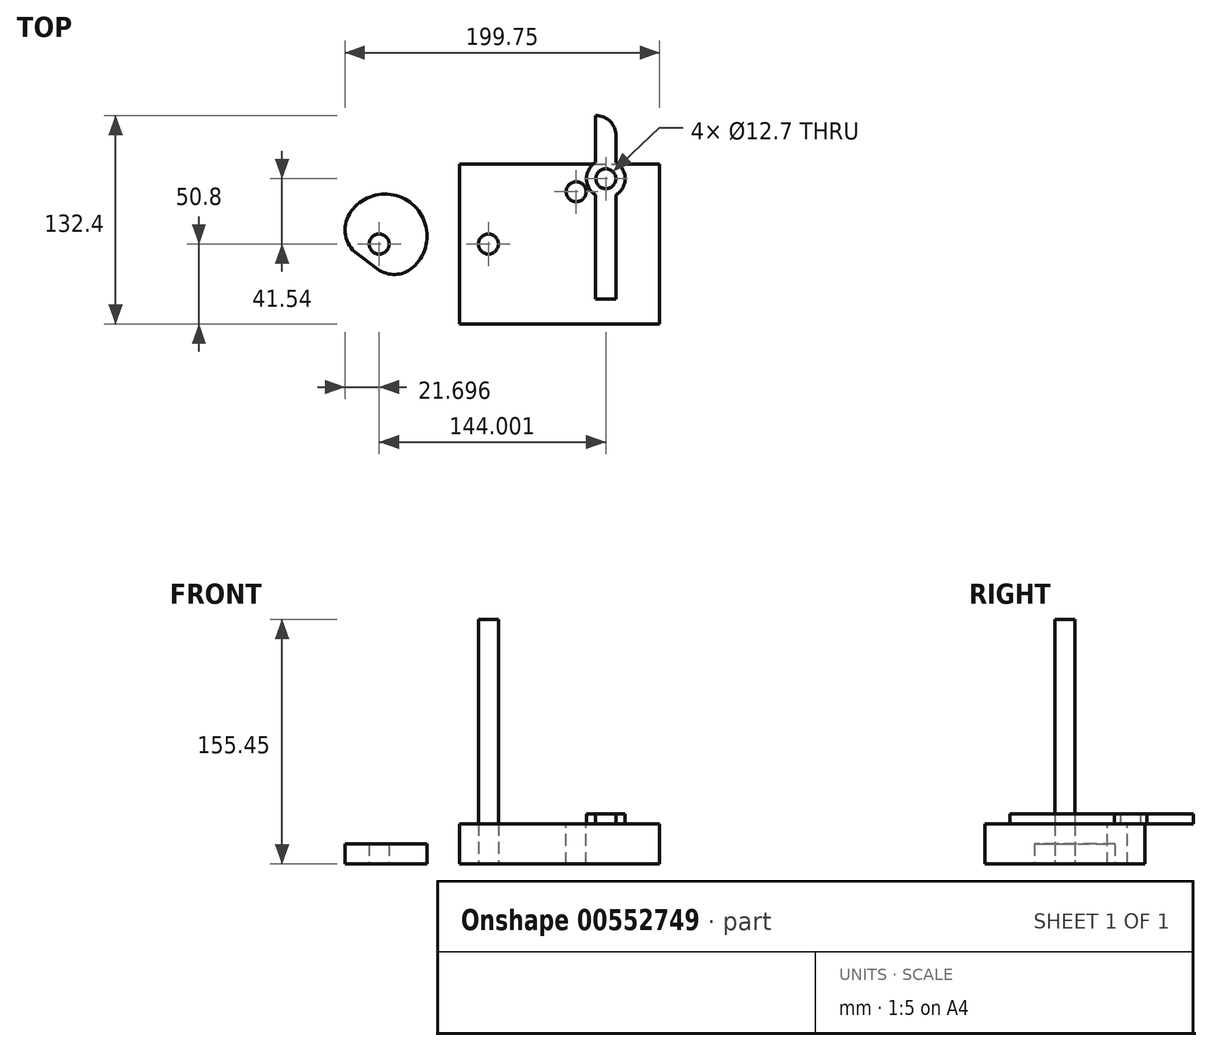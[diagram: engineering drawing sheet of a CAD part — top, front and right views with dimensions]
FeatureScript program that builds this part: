
annotation { "Feature Type Name" : "Feature", "Feature Type Description" : "" }
export const myFeature = defineFeature(function(context is Context, id is Id, definition is map)
    precondition{}
    {
        {
            var Q0;
            Q0=qCreatedBy(makeId("Top.planeOp"),FACE);
            var sketch = newSketch(context, id + "F0", { "sketchPlane" : qUnion([Q0])});
            skLineSegment(sketch, "E0.bottom", {"start": v(-63.5, -50.8) * mm, "end": v(63.5, -50.8) * mm});
            skLineSegment(sketch, "E0.top", {"start": v(-63.5, 50.8) * mm, "end": v(63.5, 50.8) * mm});
            skLineSegment(sketch, "E0.left", {"start": v(-63.5, -50.8) * mm, "end": v(-63.5, 50.8) * mm});
            skLineSegment(sketch, "E0.right", {"start": v(63.5, -50.8) * mm, "end": v(63.5, 50.8) * mm});
            skPoint(sketch, "E0.middle", {"position": v(0, 0) * mm});
            skCircle(sketch, "E1", {"center": v(-45.14, 0) * mm, "radius": 6.35 * mm});
            skSolve(sketch);
        }
        {
            var Q0;
            Q0=makeQuery(id+"F0.imprint","IMPRINT",FACE,{"disambiguationData":[TD([[makeQuery(id+"F0.imprint","IMPRINT",EDGE,{"derivedFrom":sQuery(id+"F0.wireOp",EDGE,"E0.bottom")}),1.0]])]});
            extrude(context, id + "F1", {"entities" : qUnion([Q0]), "depth" : 25.4 * mm, "offsetDistance" : 25.4 * mm});
        }
        {
            var Q0;
            Q0=makeQuery(id+"F1.opExtrude","CAP_FACE",FACE,{"disambiguationData":[OSD([sQuery(id+"F0.wireOp",EDGE,"E0.bottom"),sQuery(id+"F0.wireOp",EDGE,"E0.top"),sQuery(id+"F0.wireOp",EDGE,"E0.left"),sQuery(id+"F0.wireOp",EDGE,"E0.right"),sQuery(id+"F0.wireOp",EDGE,"E1")])],"isStart":false});
            var sketch = newSketch(context, id + "F2", { "sketchPlane" : qUnion([Q0])});
            skCircle(sketch, "E2.0", {"center": v(-45.14, 0) * mm, "radius": 6.35 * mm});
            skSolve(sketch);
        }
        {
            var Q0;
            Q0 = qSketchRegion(id + "F2", true);
            extrude(context, id + "F3", {"entities" : qUnion([Q0]), "depth" : 130.05 * mm, "offsetDistance" : 25.4 * mm});
        }
        {
            var Q0;
            Q0=qCreatedBy(makeId("Top.planeOp"),FACE);
            var sketch = newSketch(context, id + "F4", { "sketchPlane" : qUnion([Q0])});
            skArc(sketch, "E3", {"start": v(-108.1, -21.4) * mm, "mid": v(-101.23, 17.94) * mm, "end": v(-136.9, 0) * mm, "construction": true});
            skCircle(sketch, "E4", {"center": v(-114.55, 0) * mm, "radius": 6.35 * mm});
            skLineSegment(sketch, "E5", {"start": v(-136.9, 0) * mm, "end": v(-108.1, -21.4) * mm});
            skArc(sketch, "E6", {"start": v(-108.1, -21.4) * mm, "mid": v(-94.9, 26.48) * mm, "end": v(-136.9, 0) * mm});
            skSolve(sketch);
        }
        {
            var Q0;
            Q0=makeQuery(id+"F4.imprint","IMPRINT",FACE,{"disambiguationData":[TD([[makeQuery(id+"F4.imprint","IMPRINT",EDGE,{"derivedFrom":sQuery(id+"F4.wireOp",EDGE,"E4")}),-1.0]])]});
            extrude(context, id + "F5", {"entities" : qUnion([Q0]), "depth" : 12.7 * mm, "offsetDistance" : 25.4 * mm});
        }
        {
            var Q0;
            {var subQ0=sQuery(id+"F4.wireOp",EDGE,"E6");var subQ1=sQuery(id+"F4.wireOp",EDGE,"E5");Q0=makeQuery(id+"F5.opExtrude","SWEPT_EDGE",EDGE,{"disambiguationData":[OSD([subQ1,subQ0]),TDD([makeQuery(id+"F4.imprint","INTERSECT",VERTEX,{"disambiguationData":[OD(0.0)],"derivedFrom":[subQ1,subQ0]})])]});}
            fillet(context, id + "F6", {"entities" : qUnion([Q0]), "radius" : 19.05 * mm, "tangentPropagation" : true, "allowEdgeOverflow" : false});
        }
        {
            var Q0;
            {var subQ0=sQuery(id+"F4.wireOp",EDGE,"E6");var subQ1=sQuery(id+"F4.wireOp",EDGE,"E5");Q0=makeQuery(id+"F5.opExtrude","SWEPT_EDGE",EDGE,{"disambiguationData":[OSD([subQ1,subQ0]),TDD([makeQuery(id+"F4.imprint","INTERSECT",VERTEX,{"disambiguationData":[OD(1.0)],"derivedFrom":[subQ1,subQ0]})])]});}
            fillet(context, id + "F7", {"entities" : qUnion([Q0]), "radius" : 17.78 * mm, "tangentPropagation" : true, "allowEdgeOverflow" : false});
        }
        {
            var Q0;
            Q0=makeQuery(id+"F1.opExtrude","CAP_FACE",FACE,{"disambiguationData":[OSD([sQuery(id+"F0.wireOp",EDGE,"E0.bottom"),sQuery(id+"F0.wireOp",EDGE,"E0.top"),sQuery(id+"F0.wireOp",EDGE,"E0.left"),sQuery(id+"F0.wireOp",EDGE,"E0.right"),sQuery(id+"F0.wireOp",EDGE,"E1")])],"isStart":false});
            var sketch = newSketch(context, id + "F8", { "sketchPlane" : qUnion([Q0])});
            skCircle(sketch, "E7", {"center": v(10.6, 33.26) * mm, "radius": 6.35 * mm});
            skSolve(sketch);
        }
        {
            var Q0;
            Q0=makeQuery(id+"F8.imprint","IMPRINT",FACE,{"disambiguationData":[TD([[makeQuery(id+"F8.imprint","IMPRINT",EDGE,{"derivedFrom":sQuery(id+"F8.wireOp",EDGE,"E7")}),1.0]])]});
            extrude(context, id + "F9", {"entities" : qUnion([Q0]), "operationType" : NewBodyOperationType.REMOVE, "oppositeDirection" : true, "depth" : 137.92 * mm, "offsetDistance" : 25.4 * mm});
        }
        {
            var Q0;
            Q0=makeQuery(id+"F1.opExtrude","CAP_FACE",FACE,{"disambiguationData":[OSD([sQuery(id+"F0.wireOp",EDGE,"E0.bottom"),sQuery(id+"F0.wireOp",EDGE,"E0.top"),sQuery(id+"F0.wireOp",EDGE,"E0.left"),sQuery(id+"F0.wireOp",EDGE,"E0.right"),sQuery(id+"F0.wireOp",EDGE,"E1")])],"isStart":false});
            var sketch = newSketch(context, id + "F10", { "sketchPlane" : qUnion([Q0])});
            skLineSegment(sketch, "E8.bottom", {"start": v(22.88, 81.6) * mm, "end": v(35.98, 81.6) * mm});
            skLineSegment(sketch, "E8.top", {"start": v(22.88, -35.04) * mm, "end": v(35.98, -35.04) * mm});
            skLineSegment(sketch, "E8.left", {"start": v(22.88, 81.6) * mm, "end": v(22.88, 51.86) * mm});
            skLineSegment(sketch, "E8.right", {"start": v(35.98, 81.6) * mm, "end": v(35.98, 51.88) * mm});
            skArc(sketch, "E9", {"start": v(22.88, 51.86) * mm, "mid": v(17.21, 41.54) * mm, "end": v(22.88, 31.22) * mm});
            skLineSegment(sketch, "E10.trimOffspring", {"start": v(35.98, 31.2) * mm, "end": v(35.98, -35.04) * mm});
            skLineSegment(sketch, "E11.trimOffspring", {"start": v(22.88, 31.22) * mm, "end": v(22.88, -35.04) * mm});
            skCircle(sketch, "E12", {"center": v(29.45, 41.54) * mm, "radius": 6.35 * mm});
            skArc(sketch, "E13.trimOffspring", {"start": v(35.98, 31.2) * mm, "mid": v(41.68, 41.54) * mm, "end": v(35.98, 51.88) * mm});
            skSolve(sketch);
        }
        {
            var Q0;
            {var subQ0=sQuery(id+"F10.wireOp",EDGE,"E8.bottom");Q0=makeQuery(id+"F10.imprint","IMPRINT",FACE,{"disambiguationData":[TD([[makeQuery(id+"F10.imprint","IMPRINT",EDGE,{"derivedFrom":subQ0}),-1.0]])]});}
            var Q1;
            {var subQ0=sQuery(id+"F10.wireOp",EDGE,"E8.top");Q1=makeQuery(id+"F10.imprint","IMPRINT",FACE,{"disambiguationData":[TD([[makeQuery(id+"F10.imprint","IMPRINT",EDGE,{"derivedFrom":subQ0}),1.0]])]});}
            extrude(context, id + "F11", {"entities" : qUnion([Q0, Q1]), "depth" : 6.35 * mm, "offsetDistance" : 25.4 * mm});
        }
        {
            var Q0;
            Q0=makeQuery(id+"F11.opExtrude","SWEPT_EDGE",EDGE,{"disambiguationData":[OSD([sQuery(id+"F10.wireOp",EDGE,"E8.bottom"),sQuery(id+"F10.wireOp",EDGE,"E8.right")])]});
            fillet(context, id + "F12", {"entities" : qUnion([Q0]), "radius" : 12.7 * mm, "tangentPropagation" : true, "allowEdgeOverflow" : false});
        }
    });
